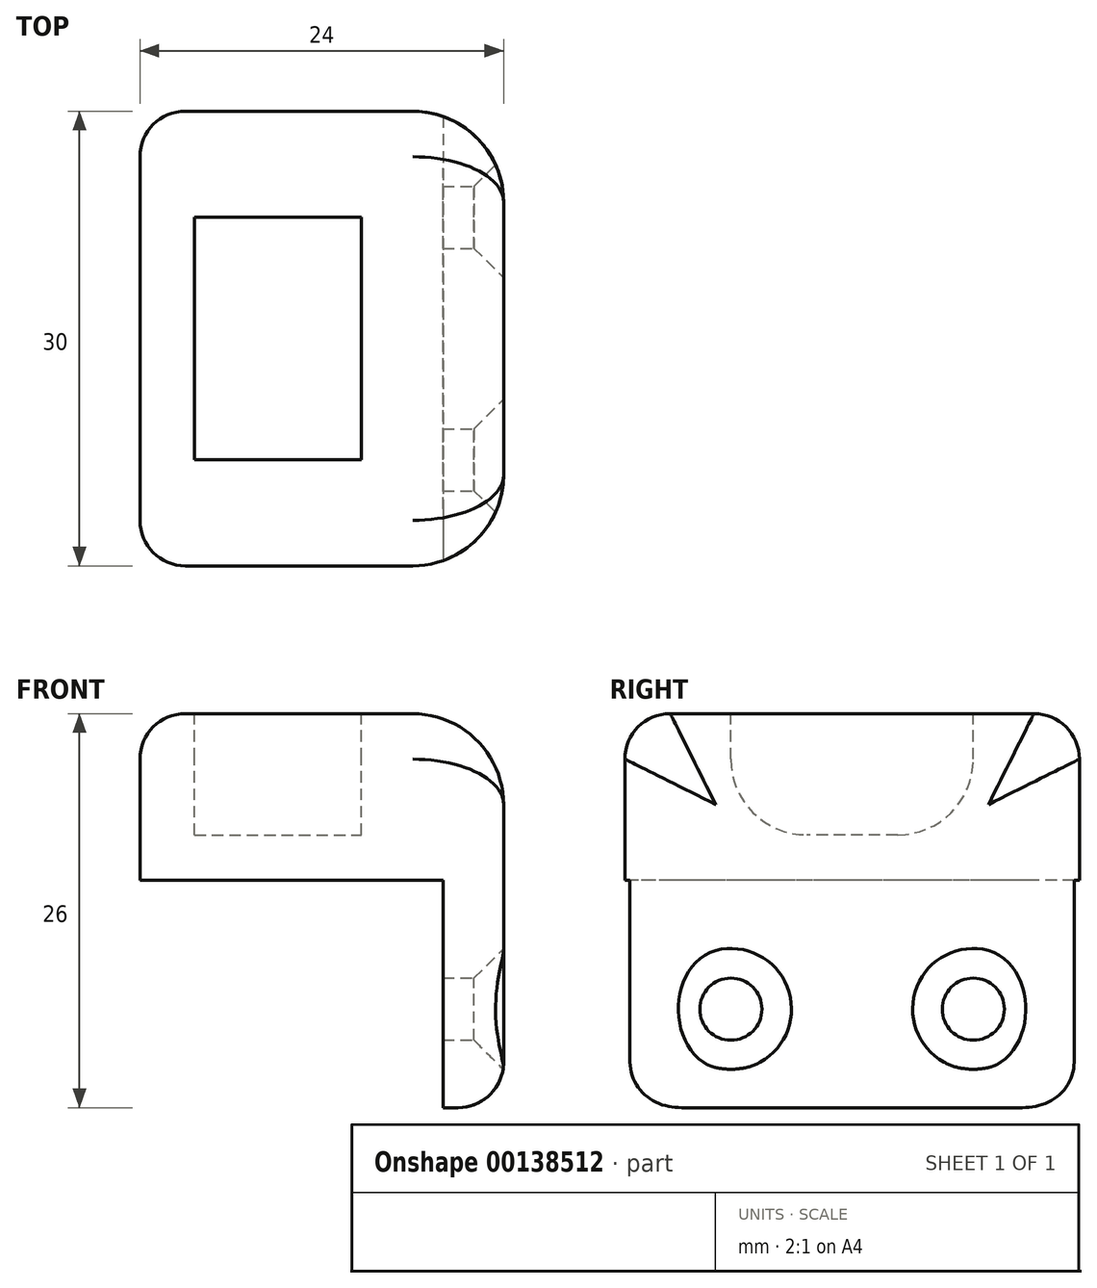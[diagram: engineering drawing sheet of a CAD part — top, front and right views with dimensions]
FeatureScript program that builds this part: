
annotation { "Feature Type Name" : "Feature", "Feature Type Description" : "" }
export const myFeature = defineFeature(function(context is Context, id is Id, definition is map)
    precondition{}
    {
        {
            var Q0;
            Q0=qCreatedBy(makeId("Right.planeOp"),FACE);
            var sketch = newSketch(context, id + "F0", { "sketchPlane" : qUnion([Q0])});
            skLineSegment(sketch, "E0.bottom", {"start": v(-15, 11) * mm, "end": v(15, 11) * mm});
            skLineSegment(sketch, "E0.top", {"start": v(-15, -15) * mm, "end": v(15, -15) * mm});
            skLineSegment(sketch, "E0.left", {"start": v(-15, 11) * mm, "end": v(-15, -15) * mm});
            skLineSegment(sketch, "E0.right", {"start": v(15, 11) * mm, "end": v(15, -15) * mm});
            skSolve(sketch);
        }
        {
            var Q0;
            Q0=qCreatedBy(makeId("Top.planeOp"),FACE);
            var sketch = newSketch(context, id + "F1", { "sketchPlane" : qUnion([Q0])});
            skLineSegment(sketch, "E1.bottom", {"start": v(-20, 15) * mm, "end": v(0, 15) * mm});
            skLineSegment(sketch, "E1.top", {"start": v(-20, -15) * mm, "end": v(0, -15) * mm});
            skLineSegment(sketch, "E1.left", {"start": v(-20, 15) * mm, "end": v(-20, -15) * mm});
            skLineSegment(sketch, "E1.right", {"start": v(0, 15) * mm, "end": v(0, -15) * mm});
            skSolve(sketch);
        }
        {
            var Q0;
            Q0 = qSketchRegion(id + "F0", true);
            extrude(context, id + "F2", {"entities" : qUnion([Q0]), "depth" : 4 * mm});
        }
        {
            var Q0;
            Q0 = qSketchRegion(id + "F1", true);
            extrude(context, id + "F3", {"entities" : qUnion([Q0]), "operationType" : NewBodyOperationType.ADD, "depth" : 11 * mm});
        }
        {
            var Q0;
            Q0=makeQuery(id+"F3.boolean.opBoolean","MERGE",FACE,{"derivedFrom":[makeQuery(id+"F2.opExtrude","SWEPT_FACE",FACE,{"disambiguationData":[OSD([sQuery(id+"F0.wireOp",EDGE,"E0.bottom")])]}),makeQuery(id+"F3.opExtrude","CAP_FACE",FACE,{"disambiguationData":[OSD([sQuery(id+"F1.wireOp",EDGE,"E1.bottom"),sQuery(id+"F1.wireOp",EDGE,"E1.top"),sQuery(id+"F1.wireOp",EDGE,"E1.left"),sQuery(id+"F1.wireOp",EDGE,"E1.right")])],"isStart":false})]});
            var sketch = newSketch(context, id + "F4", { "sketchPlane" : qUnion([Q0])});
            skLineSegment(sketch, "E2.bottom", {"start": v(-16.4, 8) * mm, "end": v(-5.4, 8) * mm});
            skLineSegment(sketch, "E2.top", {"start": v(-16.4, -8) * mm, "end": v(-5.4, -8) * mm});
            skLineSegment(sketch, "E2.left", {"start": v(-16.4, 8) * mm, "end": v(-16.4, -8) * mm});
            skLineSegment(sketch, "E2.right", {"start": v(-5.4, 8) * mm, "end": v(-5.4, -8) * mm});
            skSolve(sketch);
        }
        {
            var Q0;
            Q0 = qSketchRegion(id + "F4", true);
            extrude(context, id + "F5", {"entities" : qUnion([Q0]), "operationType" : NewBodyOperationType.REMOVE, "oppositeDirection" : true, "depth" : 8 * mm});
        }
        {
            var Q0;
            Q0=makeQuery(id+"F2.opExtrude","CAP_FACE",FACE,{"disambiguationData":[OSD([sQuery(id+"F0.wireOp",EDGE,"E0.bottom"),sQuery(id+"F0.wireOp",EDGE,"E0.top"),sQuery(id+"F0.wireOp",EDGE,"E0.left"),sQuery(id+"F0.wireOp",EDGE,"E0.right")])],"isStart":false});
            var sketch = newSketch(context, id + "F6", { "sketchPlane" : qUnion([Q0])});
            skPoint(sketch, "E3", {"position": v(-8, -8.5) * mm});
            skPoint(sketch, "E4", {"position": v(8, -8.5) * mm});
            skSolve(sketch);
        }
        {
            var Q0;
            Q0=sQuery(id+"F6.wireOp",VERTEX,"E3");
            var Q1;
            Q1=sQuery(id+"F6.wireOp",VERTEX,"E4");
            var Q2;
            Q2=makeQuery(id+"F2.opExtrude","SWEPT_BODY",BODY,{"disambiguationData":[OSD([sQuery(id+"F0.wireOp",EDGE,"E0.bottom"),sQuery(id+"F0.wireOp",EDGE,"E0.top"),sQuery(id+"F0.wireOp",EDGE,"E0.left"),sQuery(id+"F0.wireOp",EDGE,"E0.right")])]});
            hole(context, id + "F7", {"style" : HoleStyle.C_SINK, "endStyle" : HoleEndStyle.THROUGH, "holeDiameter" : 4.1 * mm, "cSinkDiameter" : 8 * mm, "cSinkAngle" : 90 * degree, "tappedDepth" : 12 * mm, "tapClearance" : 3, "locations" : qUnion([Q0, Q1]), "scope" : qUnion([Q2])});
        }
        {
            var Q0;
            Q0=makeQuery(id+"F5.boolean.opBoolean","COPY",EDGE,{"derivedFrom":makeQuery(id+"F5.opExtrude","CAP_EDGE",EDGE,{"disambiguationData":[OSD([sQuery(id+"F4.wireOp",EDGE,"E2.bottom")])],"isStart":false})});
            var Q1;
            Q1=makeQuery(id+"F5.boolean.opBoolean","COPY",EDGE,{"derivedFrom":makeQuery(id+"F5.opExtrude","CAP_EDGE",EDGE,{"disambiguationData":[OSD([sQuery(id+"F4.wireOp",EDGE,"E2.top")])],"isStart":false})});
            fillet(context, id + "F8", {"entities" : qUnion([Q0, Q1]), "radius" : 5 * mm, "tangentPropagation" : true, "allowEdgeOverflow" : false});
        }
        {
            var Q0;
            Q0=makeQuery(id+"F3.boolean.opBoolean","MERGE",EDGE,{"derivedFrom":[makeQuery(id+"F2.opExtrude","SWEPT_EDGE",EDGE,{"disambiguationData":[OSD([sQuery(id+"F0.wireOp",EDGE,"E0.bottom"),sQuery(id+"F0.wireOp",EDGE,"E0.left")])]}),makeQuery(id+"F3.opExtrude","CAP_EDGE",EDGE,{"disambiguationData":[OSD([sQuery(id+"F1.wireOp",EDGE,"E1.top")])],"isStart":false})]});
            var Q1;
            Q1=makeQuery(id+"F3.boolean.opBoolean","MERGE",EDGE,{"derivedFrom":[makeQuery(id+"F2.opExtrude","SWEPT_EDGE",EDGE,{"disambiguationData":[OSD([sQuery(id+"F0.wireOp",EDGE,"E0.bottom"),sQuery(id+"F0.wireOp",EDGE,"E0.right")])]}),makeQuery(id+"F3.opExtrude","CAP_EDGE",EDGE,{"disambiguationData":[OSD([sQuery(id+"F1.wireOp",EDGE,"E1.bottom")])],"isStart":false})]});
            var Q2;
            Q2=makeQuery(id+"F3.opExtrude","CAP_EDGE",EDGE,{"disambiguationData":[OSD([sQuery(id+"F1.wireOp",EDGE,"E1.left")])],"isStart":false});
            var Q3;
            Q3=makeQuery(id+"F3.opExtrude","SWEPT_EDGE",EDGE,{"disambiguationData":[OSD([sQuery(id+"F1.wireOp",EDGE,"E1.top"),sQuery(id+"F1.wireOp",EDGE,"E1.left")])]});
            var Q4;
            Q4=makeQuery(id+"F3.opExtrude","SWEPT_EDGE",EDGE,{"disambiguationData":[OSD([sQuery(id+"F1.wireOp",EDGE,"E1.bottom"),sQuery(id+"F1.wireOp",EDGE,"E1.left")])]});
            fillet(context, id + "F9", {"entities" : qUnion([Q0, Q1, Q2, Q3, Q4]), "radius" : 3 * mm, "tangentPropagation" : true, "allowEdgeOverflow" : false});
        }
        {
            var Q0;
            Q0=makeQuery(id+"F2.opExtrude","CAP_EDGE",EDGE,{"disambiguationData":[OSD([sQuery(id+"F0.wireOp",EDGE,"E0.bottom")])],"isStart":false});
            fillet(context, id + "F10", {"entities" : qUnion([Q0]), "radius" : 6 * mm, "tangentPropagation" : true, "allowEdgeOverflow" : false});
        }
        {
            var Q0;
            Q0=makeQuery(id+"F2.opExtrude","CAP_EDGE",EDGE,{"disambiguationData":[OSD([sQuery(id+"F0.wireOp",EDGE,"E0.top")])],"isStart":false});
            fillet(context, id + "F11", {"entities" : qUnion([Q0]), "radius" : 3 * mm, "tangentPropagation" : true, "allowEdgeOverflow" : false});
        }
    });
